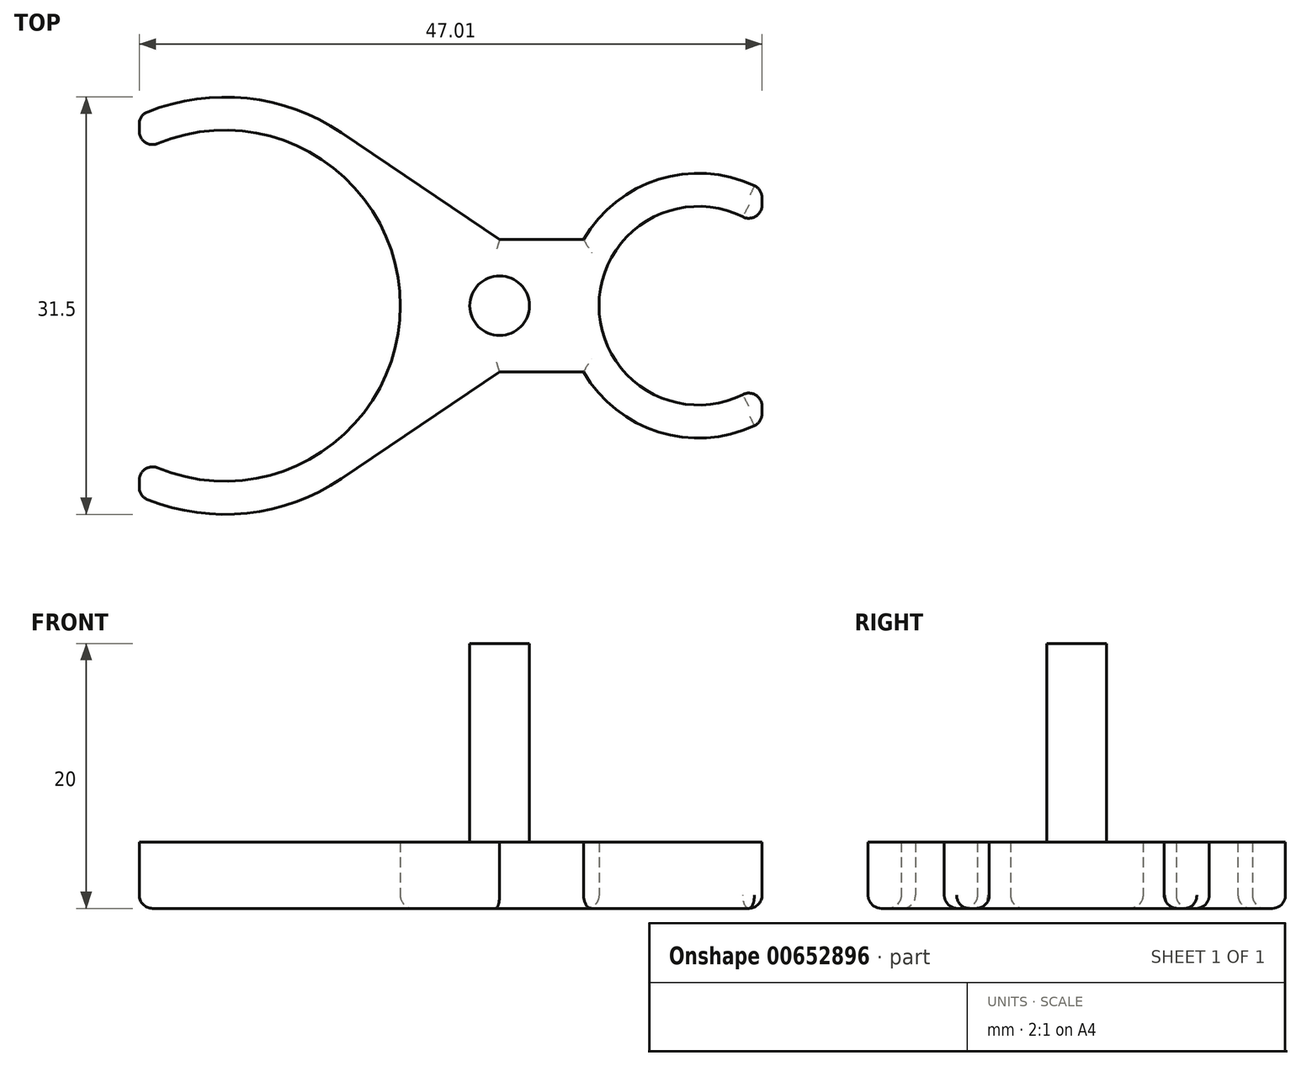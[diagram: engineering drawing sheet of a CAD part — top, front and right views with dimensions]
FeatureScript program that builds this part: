
annotation { "Feature Type Name" : "Feature", "Feature Type Description" : "" }
export const myFeature = defineFeature(function(context is Context, id is Id, definition is map)
    precondition{}
    {
        {
            var Q0;
            Q0=qCreatedBy(makeId("Top.planeOp"),FACE);
            var sketch = newSketch(context, id + "F0", { "sketchPlane" : qUnion([Q0])});
            skCircle(sketch, "E0", {"center": v(0, 0) * mm, "radius": 5 * mm});
            skCircle(sketch, "E1", {"center": v(15, 0) * mm, "radius": 10 * mm});
            skLineSegment(sketch, "E2", {"start": v(0, 5) * mm, "end": v(6.34, 5) * mm});
            skLineSegment(sketch, "E3", {"start": v(0, -5) * mm, "end": v(6.34, -5) * mm});
            skCircle(sketch, "E4.0", {"center": v(15, 0) * mm, "radius": 7.5 * mm});
            skCircle(sketch, "E5", {"center": v(-20.75, 0) * mm, "radius": 15.75 * mm});
            skLineSegment(sketch, "E6", {"start": v(0, 5) * mm, "end": v(-11.94, 13.06) * mm});
            skLineSegment(sketch, "E7", {"start": v(0, -5) * mm, "end": v(-11.94, -13.06) * mm});
            skCircle(sketch, "E8.0", {"center": v(-20.75, 0) * mm, "radius": 13.25 * mm});
            skLineSegment(sketch, "E9", {"start": v(-20.75, 0) * mm, "end": v(-20.75, -15.75) * mm});
            skSolve(sketch);
        }
        {
            var Q0;
            Q0 = qSketchRegion(id + "F0", true);
            extrude(context, id + "F1", {"entities" : qUnion([Q0]), "depth" : 5 * mm, "offsetDistance" : 25 * mm});
        }
        {
            var Q0;
            Q0=makeQuery(id+"F1.opExtrude","CAP_FACE",FACE,{"disambiguationData":[OSD([sQuery(id+"F0.wireOp",EDGE,"E1"),sQuery(id+"F0.wireOp",EDGE,"E2"),sQuery(id+"F0.wireOp",EDGE,"E3"),sQuery(id+"F0.wireOp",EDGE,"E4.0"),sQuery(id+"F0.wireOp",EDGE,"E5"),sQuery(id+"F0.wireOp",EDGE,"E6"),sQuery(id+"F0.wireOp",EDGE,"E7"),sQuery(id+"F0.wireOp",EDGE,"E8.0")])],"isStart":false});
            var sketch = newSketch(context, id + "F2", { "sketchPlane" : qUnion([Q0])});
            skCircle(sketch, "E10", {"center": v(0, 0) * mm, "radius": 2.25 * mm});
            skSolve(sketch);
        }
        {
            var Q0;
            Q0 = qSketchRegion(id + "F2", true);
            extrude(context, id + "F3", {"entities" : qUnion([Q0]), "operationType" : NewBodyOperationType.ADD, "depth" : 15 * mm, "offsetDistance" : 25 * mm});
        }
        {
            var Q0;
            Q0=makeQuery(id+"F1.opExtrude","CAP_FACE",FACE,{"disambiguationData":[OSD([sQuery(id+"F0.wireOp",EDGE,"E1"),sQuery(id+"F0.wireOp",EDGE,"E2"),sQuery(id+"F0.wireOp",EDGE,"E3"),sQuery(id+"F0.wireOp",EDGE,"E4.0"),sQuery(id+"F0.wireOp",EDGE,"E5"),sQuery(id+"F0.wireOp",EDGE,"E6"),sQuery(id+"F0.wireOp",EDGE,"E7"),sQuery(id+"F0.wireOp",EDGE,"E8.0")])],"isStart":true});
            var sketch = newSketch(context, id + "F4", { "sketchPlane" : qUnion([Q0])});
            skLineSegment(sketch, "E11", {"start": v(-27.2, 0) * mm, "end": v(-27.2, 14.37) * mm});
            skLineSegment(sketch, "E12", {"start": v(-27.2, 14.37) * mm, "end": v(-27.2, -14.37) * mm});
            skLineSegment(sketch, "E13", {"start": v(-27.2, -14.37) * mm, "end": v(-27.2, 0) * mm});
            skLineSegment(sketch, "E14.bottom", {"start": v(-27.2, -19.55) * mm, "end": v(-39.86, -19.55) * mm});
            skLineSegment(sketch, "E14.top", {"start": v(-27.2, 21.97) * mm, "end": v(-39.86, 21.97) * mm});
            skLineSegment(sketch, "E14.left", {"start": v(-27.2, -19.55) * mm, "end": v(-27.2, 21.97) * mm});
            skLineSegment(sketch, "E14.right", {"start": v(-39.86, -19.55) * mm, "end": v(-39.86, 21.97) * mm});
            skSolve(sketch);
        }
        {
            var Q0;
            Q0 = qSketchRegion(id + "F4", true);
            extrude(context, id + "F5", {"entities" : qUnion([Q0]), "operationType" : NewBodyOperationType.REMOVE, "oppositeDirection" : true, "depth" : 25 * mm, "offsetDistance" : 25 * mm});
        }
        {
            var Q0;
            Q0=makeQuery(id+"F1.opExtrude","CAP_FACE",FACE,{"disambiguationData":[OSD([sQuery(id+"F0.wireOp",EDGE,"E1"),sQuery(id+"F0.wireOp",EDGE,"E2"),sQuery(id+"F0.wireOp",EDGE,"E3"),sQuery(id+"F0.wireOp",EDGE,"E4.0"),sQuery(id+"F0.wireOp",EDGE,"E5"),sQuery(id+"F0.wireOp",EDGE,"E6"),sQuery(id+"F0.wireOp",EDGE,"E7"),sQuery(id+"F0.wireOp",EDGE,"E8.0")])],"isStart":true});
            fillet(context, id + "F6", {"entities" : qUnion([Q0]), "radius" : 1 * mm, "tangentPropagation" : true, "allowEdgeOverflow" : false});
        }
        {
            var Q0;
            Q0=makeQuery(id+"F1.opExtrude","CAP_FACE",FACE,{"disambiguationData":[OSD([sQuery(id+"F0.wireOp",EDGE,"E1"),sQuery(id+"F0.wireOp",EDGE,"E2"),sQuery(id+"F0.wireOp",EDGE,"E3"),sQuery(id+"F0.wireOp",EDGE,"E4.0"),sQuery(id+"F0.wireOp",EDGE,"E5"),sQuery(id+"F0.wireOp",EDGE,"E6"),sQuery(id+"F0.wireOp",EDGE,"E7"),sQuery(id+"F0.wireOp",EDGE,"E8.0")])],"isStart":false});
            var sketch = newSketch(context, id + "F7", { "sketchPlane" : qUnion([Q0])});
            skLineSegment(sketch, "E15.bottom", {"start": v(19.8, 17.02) * mm, "end": v(39.02, 17.02) * mm});
            skLineSegment(sketch, "E15.top", {"start": v(19.8, -14.45) * mm, "end": v(39.02, -14.45) * mm});
            skLineSegment(sketch, "E15.left", {"start": v(19.8, 17.02) * mm, "end": v(19.8, -14.45) * mm});
            skLineSegment(sketch, "E15.right", {"start": v(39.02, 17.02) * mm, "end": v(39.02, -14.45) * mm});
            skSolve(sketch);
        }
        {
            var Q0;
            Q0 = qSketchRegion(id + "F7", true);
            extrude(context, id + "F8", {"entities" : qUnion([Q0]), "operationType" : NewBodyOperationType.REMOVE, "oppositeDirection" : true, "depth" : 25 * mm, "offsetDistance" : 25 * mm});
        }
        {
            var Q0;
            Q0=makeQuery(id+"F5.boolean.opBoolean","INTERSECT",EDGE,{"disambiguationData":[OD(0.0)],"derivedFrom":[makeQuery(id+"F1.opExtrude","SWEPT_FACE",FACE,{"disambiguationData":[OSD([sQuery(id+"F0.wireOp",EDGE,"E8.0")])]}),makeQuery(id+"F5.opExtrude","SWEPT_FACE",FACE,{"disambiguationData":[OSD([sQuery(id+"F4.wireOp",EDGE,"E14.left")])]})]});
            var Q1;
            Q1=makeQuery(id+"F5.boolean.opBoolean","INTERSECT",EDGE,{"disambiguationData":[OD(1.0)],"derivedFrom":[makeQuery(id+"F1.opExtrude","SWEPT_FACE",FACE,{"disambiguationData":[OSD([sQuery(id+"F0.wireOp",EDGE,"E8.0")])]}),makeQuery(id+"F5.opExtrude","SWEPT_FACE",FACE,{"disambiguationData":[OSD([sQuery(id+"F4.wireOp",EDGE,"E14.left")])]})]});
            var Q2;
            Q2=makeQuery(id+"F5.boolean.opBoolean","INTERSECT",EDGE,{"disambiguationData":[OD(1.0)],"derivedFrom":[makeQuery(id+"F1.opExtrude","SWEPT_FACE",FACE,{"disambiguationData":[OSD([sQuery(id+"F0.wireOp",EDGE,"E5")])]}),makeQuery(id+"F5.opExtrude","SWEPT_FACE",FACE,{"disambiguationData":[OSD([sQuery(id+"F4.wireOp",EDGE,"E14.left")])]})]});
            var Q3;
            Q3=makeQuery(id+"F5.boolean.opBoolean","INTERSECT",EDGE,{"disambiguationData":[OD(0.0)],"derivedFrom":[makeQuery(id+"F1.opExtrude","SWEPT_FACE",FACE,{"disambiguationData":[OSD([sQuery(id+"F0.wireOp",EDGE,"E5")])]}),makeQuery(id+"F5.opExtrude","SWEPT_FACE",FACE,{"disambiguationData":[OSD([sQuery(id+"F4.wireOp",EDGE,"E14.left")])]})]});
            var Q4;
            Q4=makeQuery(id+"F8.boolean.opBoolean","INTERSECT",EDGE,{"disambiguationData":[OD(0.0)],"derivedFrom":[makeQuery(id+"F1.opExtrude","SWEPT_FACE",FACE,{"disambiguationData":[OSD([sQuery(id+"F0.wireOp",EDGE,"E1")])]}),makeQuery(id+"F8.opExtrude","SWEPT_FACE",FACE,{"disambiguationData":[OSD([sQuery(id+"F7.wireOp",EDGE,"E15.left")])]})]});
            var Q5;
            Q5=makeQuery(id+"F8.boolean.opBoolean","INTERSECT",EDGE,{"disambiguationData":[OD(0.0)],"derivedFrom":[makeQuery(id+"F1.opExtrude","SWEPT_FACE",FACE,{"disambiguationData":[OSD([sQuery(id+"F0.wireOp",EDGE,"E4.0")])]}),makeQuery(id+"F8.opExtrude","SWEPT_FACE",FACE,{"disambiguationData":[OSD([sQuery(id+"F7.wireOp",EDGE,"E15.left")])]})]});
            var Q6;
            Q6=makeQuery(id+"F8.boolean.opBoolean","INTERSECT",EDGE,{"disambiguationData":[OD(1.0)],"derivedFrom":[makeQuery(id+"F1.opExtrude","SWEPT_FACE",FACE,{"disambiguationData":[OSD([sQuery(id+"F0.wireOp",EDGE,"E4.0")])]}),makeQuery(id+"F8.opExtrude","SWEPT_FACE",FACE,{"disambiguationData":[OSD([sQuery(id+"F7.wireOp",EDGE,"E15.left")])]})]});
            fillet(context, id + "F9", {"entities" : qUnion([Q0, Q1, Q2, Q3, Q4, Q5, Q6]), "radius" : 1 * mm, "tangentPropagation" : true, "allowEdgeOverflow" : false});
        }
    });
